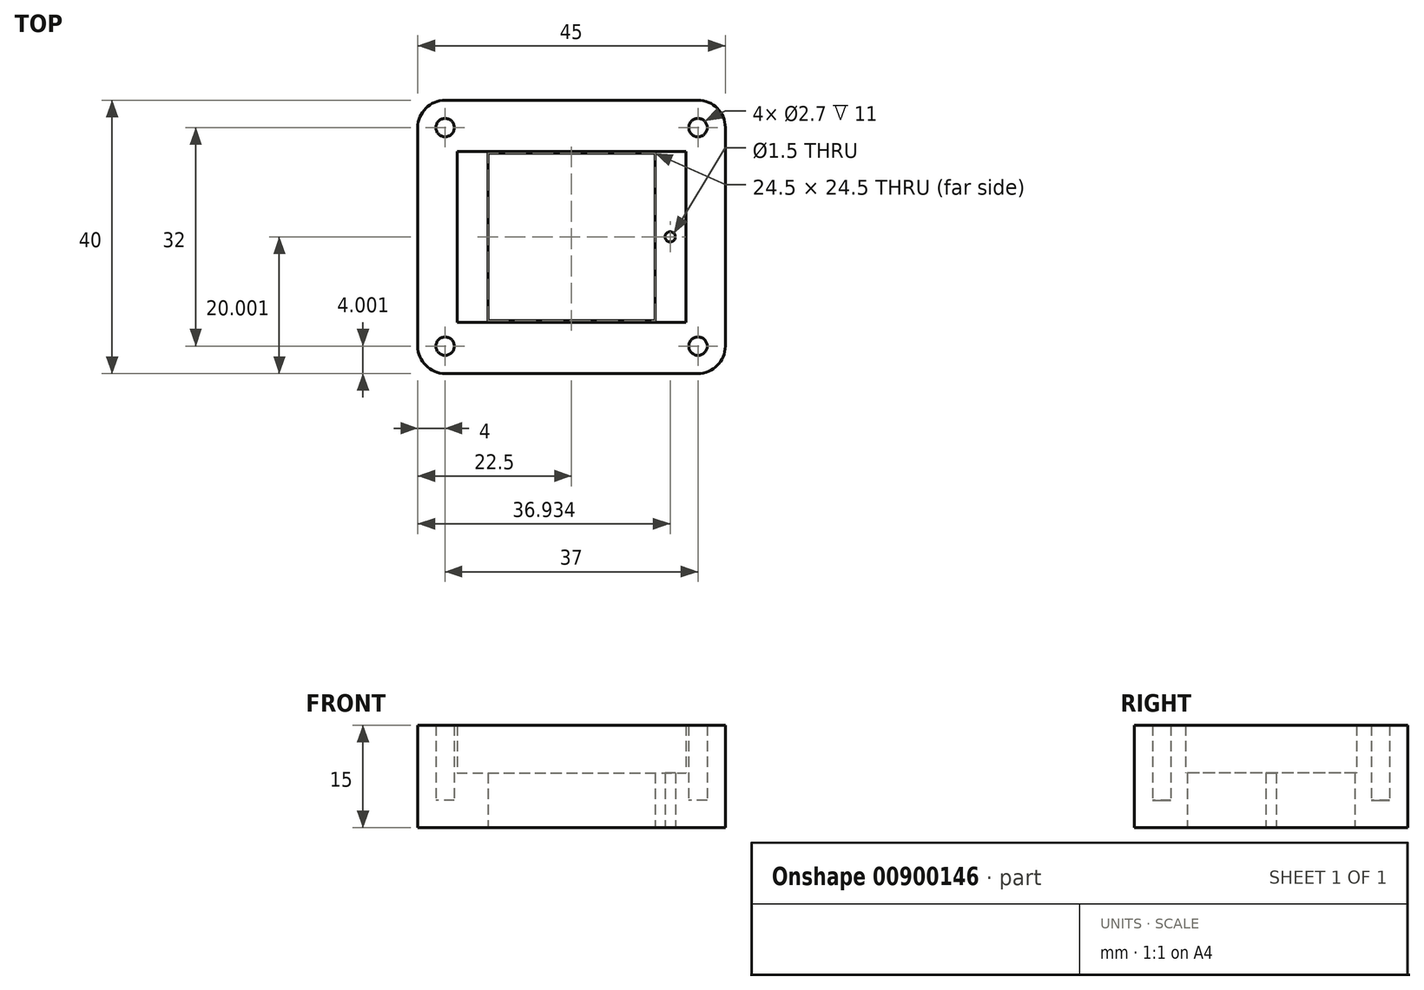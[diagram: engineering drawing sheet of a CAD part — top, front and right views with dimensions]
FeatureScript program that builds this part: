
annotation { "Feature Type Name" : "Feature", "Feature Type Description" : "" }
export const myFeature = defineFeature(function(context is Context, id is Id, definition is map)
    precondition{}
    {
        {
            var Q0;
            Q0=qCreatedBy(makeId("Top.planeOp"),FACE);
            var sketch = newSketch(context, id + "F0", { "sketchPlane" : qUnion([Q0])});
            skLineSegment(sketch, "E0", {"start": v(-24.74, 11.73) * mm, "end": v(-24.74, -20.27) * mm});
            skLineSegment(sketch, "E1", {"start": v(-20.74, -24.27) * mm, "end": v(16.26, -24.27) * mm});
            skLineSegment(sketch, "E2", {"start": v(20.26, -20.27) * mm, "end": v(20.26, 11.73) * mm});
            skLineSegment(sketch, "E3", {"start": v(16.26, 15.73) * mm, "end": v(-20.74, 15.73) * mm});
            skPoint(sketch, "E4.visualSharp", {"position": v(-24.74, 15.73) * mm});
            skArc(sketch, "E4.filletArc", {"start": v(-20.74, 15.73) * mm, "mid": v(-23.57, 14.56) * mm, "end": v(-24.74, 11.73) * mm});
            skPoint(sketch, "E5.visualSharp", {"position": v(20.26, 15.73) * mm});
            skArc(sketch, "E5.filletArc", {"start": v(20.26, 11.73) * mm, "mid": v(19.09, 14.56) * mm, "end": v(16.26, 15.73) * mm});
            skPoint(sketch, "E6.visualSharp", {"position": v(20.26, -24.27) * mm});
            skArc(sketch, "E6.filletArc", {"start": v(16.26, -24.27) * mm, "mid": v(19.09, -23.1) * mm, "end": v(20.26, -20.27) * mm});
            skPoint(sketch, "E7.visualSharp", {"position": v(-24.74, -24.27) * mm});
            skArc(sketch, "E7.filletArc", {"start": v(-24.74, -20.27) * mm, "mid": v(-23.57, -23.1) * mm, "end": v(-20.74, -24.27) * mm});
            skCircle(sketch, "E8", {"center": v(16.26, -20.27) * mm, "radius": 1.35 * mm});
            skCircle(sketch, "E9", {"center": v(16.26, 11.73) * mm, "radius": 1.35 * mm});
            skCircle(sketch, "E10", {"center": v(-20.74, 11.73) * mm, "radius": 1.35 * mm});
            skCircle(sketch, "E11", {"center": v(-20.74, -20.27) * mm, "radius": 1.35 * mm});
            skLineSegment(sketch, "E12.bottom", {"start": v(-14.5, 7.98) * mm, "end": v(10, 7.98) * mm});
            skLineSegment(sketch, "E12.top", {"start": v(-14.5, -16.52) * mm, "end": v(10, -16.52) * mm});
            skLineSegment(sketch, "E12.left", {"start": v(-14.5, 7.98) * mm, "end": v(-14.5, -16.52) * mm});
            skLineSegment(sketch, "E12.right", {"start": v(10, 7.98) * mm, "end": v(10, -16.52) * mm});
            skLineSegment(sketch, "E13.bottom", {"start": v(-19, 8.23) * mm, "end": v(14.5, 8.23) * mm});
            skLineSegment(sketch, "E13.top", {"start": v(-19, -16.77) * mm, "end": v(14.5, -16.77) * mm});
            skLineSegment(sketch, "E13.left", {"start": v(-19, 8.23) * mm, "end": v(-19, -16.77) * mm});
            skLineSegment(sketch, "E13.right", {"start": v(14.5, 8.23) * mm, "end": v(14.5, -16.77) * mm});
            skLineSegment(sketch, "E14", {"start": v(-19, -4.27) * mm, "end": v(14.5, -4.27) * mm, "construction": true});
            skLineSegment(sketch, "E15", {"start": v(-16.67, 8.23) * mm, "end": v(-16.67, -16.77) * mm, "construction": true});
            skCircle(sketch, "E16", {"center": v(-16.67, -4.27) * mm, "radius": 0.75 * mm});
            skLineSegment(sketch, "E17", {"start": v(-2.24, 8.23) * mm, "end": v(-2.24, -16.77) * mm, "construction": true});
            skCircle(sketch, "E18.MirrorC", {"center": v(12.2, -4.27) * mm, "radius": 0.75 * mm});
            skSolve(sketch);
        }
        {
            var Q0;
            Q0 = qSketchRegion(id + "F0", true);
            extrude(context, id + "F1", {"entities" : qUnion([Q0]), "depth" : 15 * mm, "offsetDistance" : 25 * mm});
        }
        {
            var Q0;
            Q0=makeQuery(id+"F0.imprint","IMPRINT",FACE,{"disambiguationData":[TD([[makeQuery(id+"F0.imprint","IMPRINT",EDGE,{"derivedFrom":sQuery(id+"F0.wireOp",EDGE,"E12.bottom")}),1.0]])]});
            extrude(context, id + "F2", {"entities" : qUnion([Q0]), "operationType" : NewBodyOperationType.ADD, "depth" : 3 * mm, "offsetDistance" : 25 * mm});
        }
        {
            var Q0;
            Q0=makeQuery(id+"F0.imprint","IMPRINT",FACE,{"disambiguationData":[TD([[makeQuery(id+"F0.imprint","IMPRINT",EDGE,{"derivedFrom":sQuery(id+"F0.wireOp",EDGE,"E16")}),1.0]])]});
            var Q1;
            Q1=makeQuery(id+"F0.imprint","IMPRINT",FACE,{"disambiguationData":[TD([[makeQuery(id+"F0.imprint","IMPRINT",EDGE,{"derivedFrom":sQuery(id+"F0.wireOp",EDGE,"E18.MirrorC")}),-1.0]])]});
            extrude(context, id + "F3", {"entities" : qUnion([Q0, Q1]), "operationType" : NewBodyOperationType.ADD, "depth" : 8 * mm, "offsetDistance" : 25 * mm});
        }
        {
            var Q0;
            Q0=makeQuery(id+"F0.imprint","IMPRINT",FACE,{"disambiguationData":[TD([[makeQuery(id+"F0.imprint","IMPRINT",EDGE,{"derivedFrom":sQuery(id+"F0.wireOp",EDGE,"E10")}),1.0]])]});
            var Q1;
            Q1=makeQuery(id+"F0.imprint","IMPRINT",FACE,{"disambiguationData":[TD([[makeQuery(id+"F0.imprint","IMPRINT",EDGE,{"derivedFrom":sQuery(id+"F0.wireOp",EDGE,"E9")}),1.0]])]});
            var Q2;
            Q2=makeQuery(id+"F0.imprint","IMPRINT",FACE,{"disambiguationData":[TD([[makeQuery(id+"F0.imprint","IMPRINT",EDGE,{"derivedFrom":sQuery(id+"F0.wireOp",EDGE,"E8")}),1.0]])]});
            var Q3;
            Q3=makeQuery(id+"F0.imprint","IMPRINT",FACE,{"disambiguationData":[TD([[makeQuery(id+"F0.imprint","IMPRINT",EDGE,{"derivedFrom":sQuery(id+"F0.wireOp",EDGE,"E11")}),1.0]])]});
            extrude(context, id + "F4", {"entities" : qUnion([Q0, Q1, Q2, Q3]), "operationType" : NewBodyOperationType.ADD, "depth" : 4 * mm, "offsetDistance" : 25 * mm});
        }
    });
